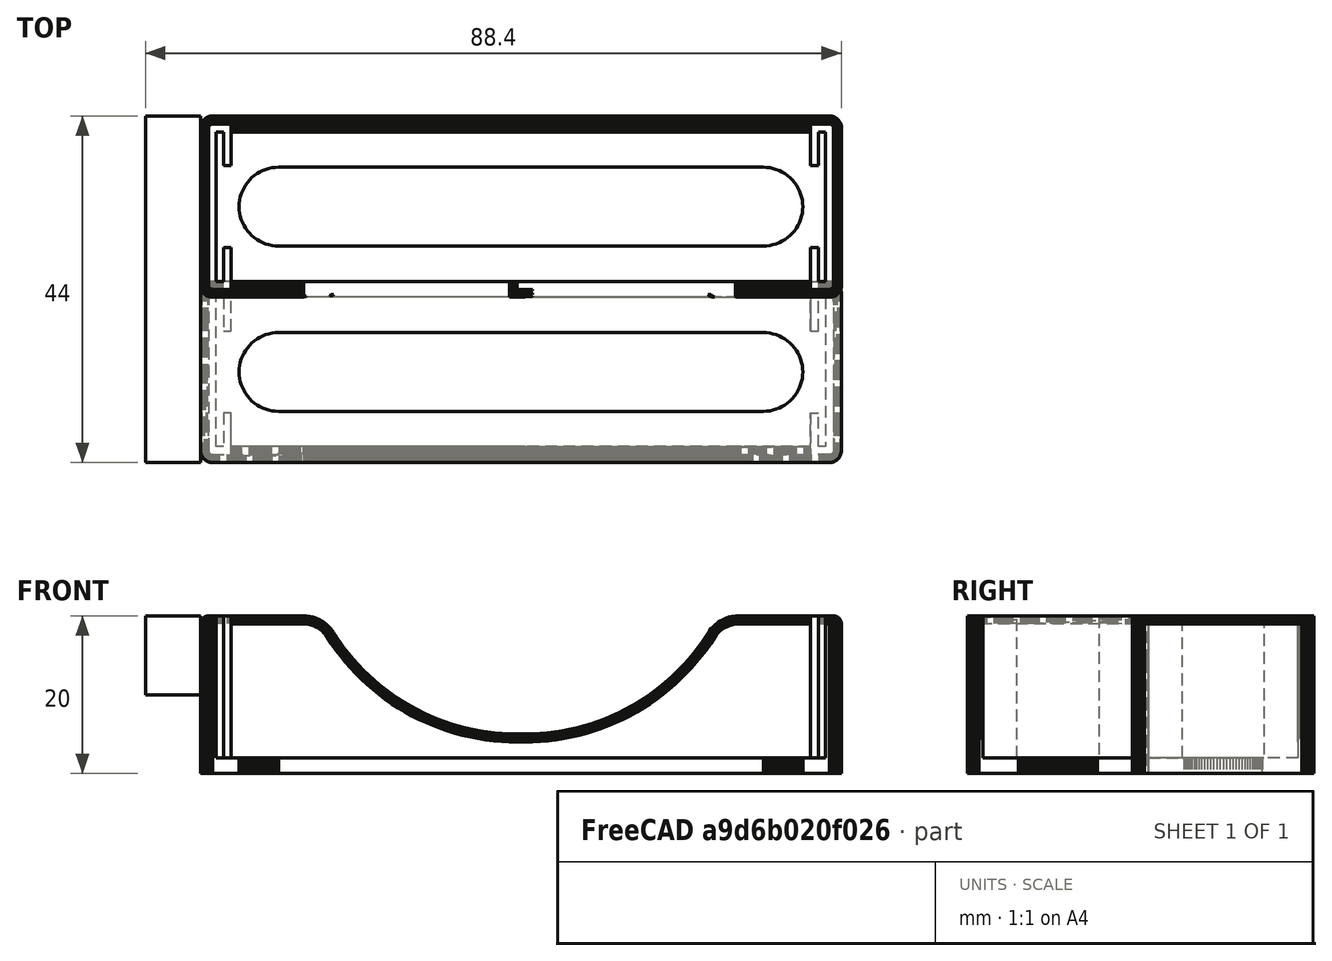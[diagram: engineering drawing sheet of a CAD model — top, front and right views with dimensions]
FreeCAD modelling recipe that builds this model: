
FCSTD DOCUMENT  (FreeCAD 0.21R33771 (Git))
Label: battery mk4
License: All rights reserved
LicenseURL: https://en.wikipedia.org/wiki/All_rights_reserved
objects: App::MeasureDistance×11, Part::Feature×3, PartDesign::Body×3, Sketcher::SketchObject×2, PartDesign::Pad×1, App::Part×1
note: 10 computed .brp shape members not serialized (recipe doc carries the construction recipe); baked Part::Feature solids carry a one-line shape summary decoded from their .brp

FEATURE [Part::Feature] __Batterie_2_001  label="batt_group_2"
  shape: bbox 81.4 x 44 x 20 mm, 17624 faces, 0 solids (baked)
FEATURE [Sketcher::SketchObject] Sketch  label="btm row conn piece"
  FullyConstrained = false
  MapMode = 5
  Placement = pos=(0,0,0) rot=(0.57735,0.57735,0.57735;2.0944rad)
  Support = -> [YZ_Plane]
  sketch-geometry (4):
    g0: LineSegment StartX=44 StartY=20 StartZ=0 EndX=0 EndY=20 EndZ=0
    g1: LineSegment StartX=0 StartY=20 StartZ=0 EndX=0 EndY=10 EndZ=0
    g2: LineSegment StartX=0 StartY=10 StartZ=0 EndX=44 EndY=10 EndZ=0
    g3: LineSegment StartX=44 StartY=10 StartZ=0 EndX=44 EndY=20 EndZ=0
  constraints (10):
    c: Coincident(g0,g1)
    c: Coincident(g1,g2)
    c: Coincident(g2,g3)
    c: Coincident(g3,g0)
    c: Horizontal(g0)
    c: Horizontal(g2)
    c: Vertical(g1)
    c: Vertical(g3)
    c: DistanceX(g0,g0) = 44
    c: DistanceY(g3,g3) = 10
FEATURE [PartDesign::Pad] Pad
  Direction = (1,-2e-16,3e-16)
  Length = 7
  Length2 = 10
  Placement = pos=(0,0,0) rot=(0.57735,0.57735,0.57735;2.0944rad)
  Profile = -> Sketch
  ReferenceAxis = -> Sketch [N_Axis]
  Reversed = true
  Type = 0
FEATURE [PartDesign::Body] Body  label="bottom row centre"
  Group = -> [Sketch,Pad]
  Origin = -> Origin
  Tip = -> Pad
FEATURE [PartDesign::Body] Body001  label="Body"
  Origin = -> Origin002
FEATURE [Part::Feature] __Batterie_2_002  label="batt_group_1"
  Placement = pos=(-7,44,0) rot=(0,0,1;3.14159rad)
  shape: bbox 81.4 x 44 x 20 mm, 17624 faces, 0 solids (baked)
FEATURE [Sketcher::SketchObject] Sketch002  label="bottom plating"
  FullyConstrained = false
  MapMode = 5
  Support = -> [XY_Plane003]
  sketch-geometry (8):
    g0: LineSegment StartX=4.8015 StartY=6.4 StartZ=0 EndX=76.9015 EndY=6.4 EndZ=0
    g1: LineSegment StartX=76.9015 StartY=6.4 StartZ=0 EndX=76.9015 EndY=38 EndZ=0
    g2: LineSegment StartX=76.9015 StartY=38 StartZ=0 EndX=4.8015 EndY=38 EndZ=0
    g3: LineSegment StartX=4.8015 StartY=38 StartZ=0 EndX=4.8015 EndY=6.4 EndZ=0
    g4: LineSegment StartX=93 StartY=6.4 StartZ=0 EndX=165.2 EndY=6.4 EndZ=0
    g5: LineSegment StartX=165.2 StartY=6.4 StartZ=0 EndX=165.2 EndY=37.8 EndZ=0
    g6: LineSegment StartX=165.2 StartY=37.8 StartZ=0 EndX=93 EndY=37.8 EndZ=0
    g7: LineSegment StartX=93 StartY=37.8 StartZ=0 EndX=93 EndY=6.4 EndZ=0
  constraints (20):
    c: Coincident(g0,g1)
    c: Coincident(g1,g2)
    c: Coincident(g2,g3)
    c: Coincident(g3,g0)
    c: Horizontal(g0)
    c: Horizontal(g2)
    c: Vertical(g1)
    c: Vertical(g3)
    c: Coincident(g4,g5)
    c: Coincident(g5,g6)
    c: Coincident(g6,g7)
    c: Coincident(g7,g4)
    c: Horizontal(g4)
    c: Horizontal(g6)
    c: Vertical(g5)
    c: Vertical(g7)
    c: DistanceY(g5,g5) = 31.4
    c: DistanceX(g4,g4) = 72.2
    c: DistanceX(g0,g0) = 72.1
    c: DistanceY(g1,g1) = 31.6
FEATURE [PartDesign::Body] Body002  label="bottom row flooring"
  Group = -> [Sketch002]
  Origin = -> Origin003
  Placement = pos=(-88.35,0,0) rot=(0,0,1;0rad)
FEATURE [App::Part] Part  label="bottom row battery group"
  Group = -> [Body,__Batterie_2_001,Body001,__Batterie_2_002,Body002]
  Origin = -> Origin001
FEATURE [Part::Feature] __Batterie_2_001_solid  label="batt_group_2 (Solid)"
  shape: bbox 81.4 x 44 x 20 mm, 17624 faces (baked)
FEATURE [App::MeasureDistance] Distance  label="Distance: 19.00 mm"
  Distance = 19
  P1 = (-86.3701,21,20)
  P2 = (-86.35,2,20)
FEATURE [App::MeasureDistance] Distance001  label="Distance: 0.85 mm"
  Distance = 0.847339
  P1 = (-86.325,21,20)
  P2 = (-85.4789,20.9543,20)
FEATURE [App::MeasureDistance] Distance002  label="Distance: 10.44 mm"
  Distance = 10.4378
  P1 = (-85.4486,16.7,20)
  P2 = (-85.4983,6.26236,20)
FEATURE [App::MeasureDistance] Distance003  label="Distance: 4.29 mm"
  Distance = 4.29454
  P1 = (-85.4721,20.9945,20)
  P2 = (-85.4793,16.7,20)
FEATURE [App::MeasureDistance] Distance004  label="Distance: 1.01 mm"
  Distance = 1.01343
  P1 = (-86.3358,1.97223,20)
  P2 = (-86.1914,0.969131,19.9981)
FEATURE [App::MeasureDistance] Distance005  label="Distance: 73.61 mm"
  Distance = 73.607
  P1 = (-84.5,6.2685,20)
  P2 = (-10.893,6.29557,20)
FEATURE [App::MeasureDistance] Distance006  label="Distance: 2.02 mm"
  Distance = 2.02389
  P1 = (79.4,20.9821,20)
  P2 = (81.2788,20.4426,19.4755)
FEATURE [App::MeasureDistance] Distance007  label="Distance: 19.77 mm"
  Distance = 19.7676
  P1 = (-86.9,0,0)
  P2 = (-86.7954,0.355179,19.7642)
FEATURE [App::MeasureDistance] Distance008  label="Distance: 18.00 mm"
  Distance = 18
  P1 = (-84.4906,27.3003,2)
  P2 = (-84.5,27.3,20)
FEATURE [App::MeasureDistance] Distance009  label="Distance: 78.74 mm"
  Distance = 78.7398
  P1 = (-87.0697,1.01958,19.9991)
  P2 = (-8.32996,1.0216,19.9993)
FEATURE [App::MeasureDistance] Distance010  label="Distance: 18.87 mm"
  Distance = 18.8655
  P1 = (-10.9,23.0099,20)
  P2 = (-10.9,41.8754,20)
